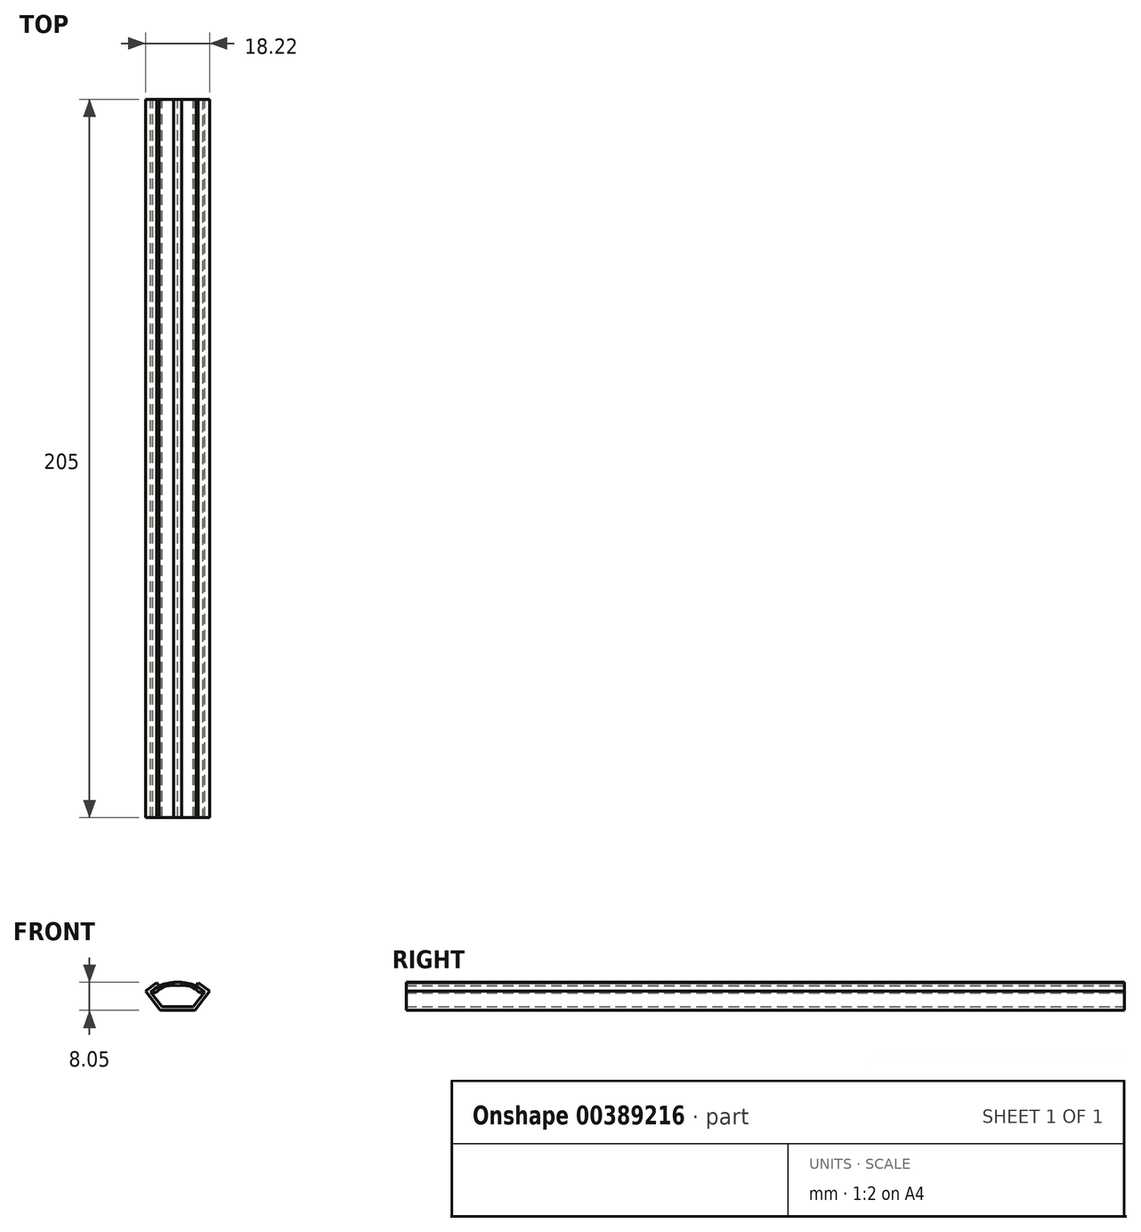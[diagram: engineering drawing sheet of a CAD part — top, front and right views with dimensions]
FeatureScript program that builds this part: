
annotation { "Feature Type Name" : "Feature", "Feature Type Description" : "" }
export const myFeature = defineFeature(function(context is Context, id is Id, definition is map)
    precondition{}
    {
        {
            var Q0;
            Q0=qCreatedBy(makeId("Front.planeOp"),FACE);
            var sketch = newSketch(context, id + "F0", { "sketchPlane" : qUnion([Q0])});
            skLineSegment(sketch, "E0", {"start": v(0, -6.08) * mm, "end": v(-4.5, -6.08) * mm});
            skLineSegment(sketch, "E1", {"start": v(-4.5, -6.08) * mm, "end": v(-7.7, -1.8) * mm});
            skLineSegment(sketch, "E2", {"start": v(-7.7, -1.8) * mm, "end": v(-5.3, 0) * mm});
            skLineSegment(sketch, "E3", {"start": v(-5.3, 0) * mm, "end": v(-5.9, 0.8) * mm});
            skLineSegment(sketch, "E4", {"start": v(-5.9, 0.8) * mm, "end": v(-9.1, -1.6) * mm});
            skLineSegment(sketch, "E5", {"start": v(-9.1, -1.6) * mm, "end": v(-5, -7.08) * mm});
            skLineSegment(sketch, "E6", {"start": v(-5, -7.08) * mm, "end": v(0, -7.08) * mm});
            skLineSegment(sketch, "E7.MirrorCS", {"start": v(5.3, 0) * mm, "end": v(5.9, 0.8) * mm});
            skLineSegment(sketch, "E8.MirrorCS", {"start": v(5.9, 0.8) * mm, "end": v(9.1, -1.6) * mm});
            skLineSegment(sketch, "E9.MirrorCS", {"start": v(4.5, -6.08) * mm, "end": v(7.7, -1.8) * mm});
            skLineSegment(sketch, "E10.MirrorCS", {"start": v(5, -7.08) * mm, "end": v(0, -7.08) * mm});
            skLineSegment(sketch, "E11.MirrorCS", {"start": v(7.7, -1.8) * mm, "end": v(5.3, 0) * mm});
            skLineSegment(sketch, "E12.MirrorCS", {"start": v(9.1, -1.6) * mm, "end": v(5, -7.08) * mm});
            skLineSegment(sketch, "E13.MirrorCS", {"start": v(0, -6.08) * mm, "end": v(4.5, -6.08) * mm});
            skSolve(sketch);
        }
        {
            var Q0;
            Q0 = qSketchRegion(id + "F0", true);
            extrude(context, id + "F1", {"entities" : qUnion([Q0]), "depth" : 205 * mm, "offsetDistance" : 25.4 * mm});
        }
        {
            var Q0;
            Q0=qCreatedBy(makeId("Front.planeOp"),FACE);
            var sketch = newSketch(context, id + "F2", { "sketchPlane" : qUnion([Q0])});
            skLineSegment(sketch, "E14", {"start": v(-1.2, 0.97) * mm, "end": v(0, 0.97) * mm});
            skFitSpline(sketch, "E15", {"points": [v(-1.2, 0.97) * mm, v(-4.94, 0) * mm, v(-7.14, -1.73) * mm, v(-6.47, -2.04) * mm, v(-4.26, -0.5) * mm, v(0, 0) * mm], "startDerivative": vector(-15.37, -2.41) * mm, "endDerivative": vector(18.48, -0.68) * mm});
            skFitSpline(sketch, "E16.MirrorCS", {"points": [v(1.2, 0.97) * mm, v(4.94, 0) * mm, v(7.14, -1.73) * mm, v(6.47, -2.04) * mm, v(4.26, -0.5) * mm, v(0, 0) * mm], "startDerivative": vector(15.37, -2.41) * mm, "endDerivative": vector(-18.48, -0.68) * mm});
            skLineSegment(sketch, "E17.MirrorCS", {"start": v(1.2, 0.97) * mm, "end": v(0, 0.97) * mm});
            skSolve(sketch);
        }
        {
            var Q0;
            Q0 = qSketchRegion(id + "F2", true);
            extrude(context, id + "F3", {"entities" : qUnion([Q0]), "depth" : 205 * mm, "offsetDistance" : 25.4 * mm});
        }
    });
